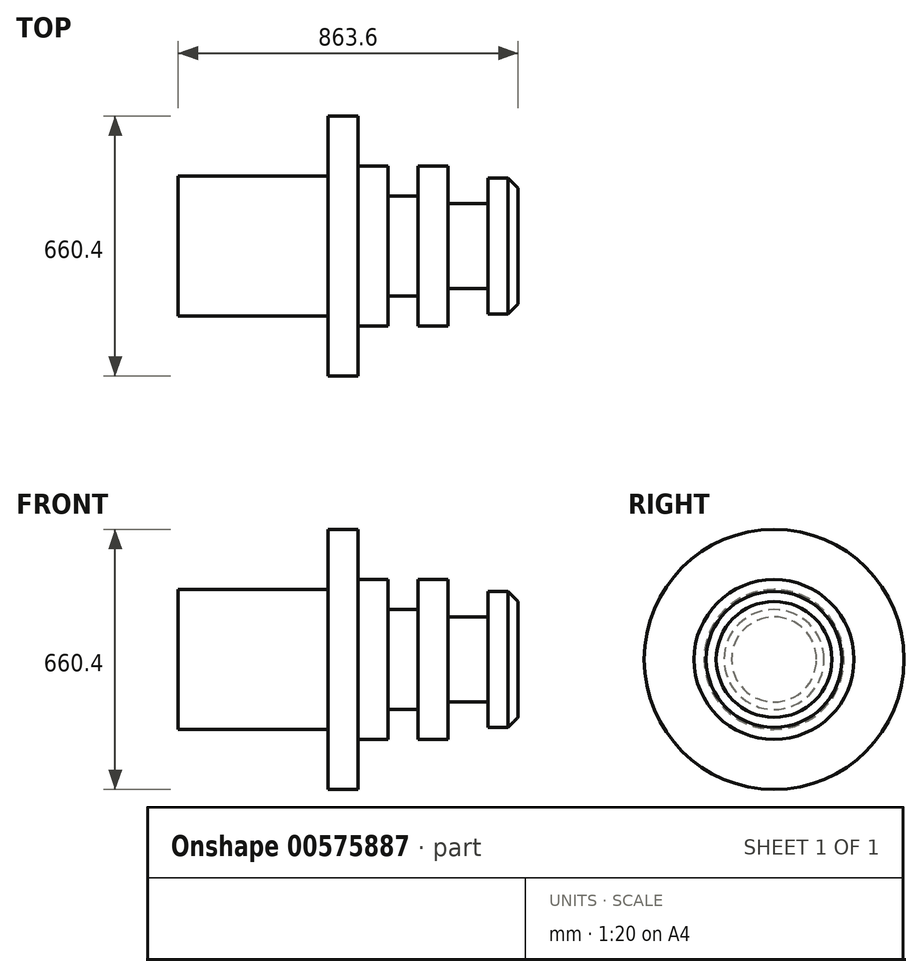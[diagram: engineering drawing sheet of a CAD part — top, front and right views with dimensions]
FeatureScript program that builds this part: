
annotation { "Feature Type Name" : "Feature", "Feature Type Description" : "" }
export const myFeature = defineFeature(function(context is Context, id is Id, definition is map)
    precondition{}
    {
        {
            var Q0;
            Q0=qCreatedBy(makeId("Front.planeOp"),FACE);
            var sketch = newSketch(context, id + "F0", { "sketchPlane" : qUnion([Q0])});
            skLineSegment(sketch, "E0", {"start": v(0, 0) * mm, "end": v(0, 177.8) * mm});
            skLineSegment(sketch, "E1", {"start": v(0, 0) * mm, "end": v(863.6, 0) * mm});
            skLineSegment(sketch, "E2", {"start": v(0, 177.8) * mm, "end": v(381, 177.8) * mm});
            skLineSegment(sketch, "E3", {"start": v(381, 177.8) * mm, "end": v(381, 330.2) * mm});
            skLineSegment(sketch, "E4", {"start": v(381, 330.2) * mm, "end": v(457.2, 330.2) * mm});
            skLineSegment(sketch, "E5", {"start": v(457.2, 330.2) * mm, "end": v(457.2, 203.2) * mm});
            skLineSegment(sketch, "E6", {"start": v(457.2, 203.2) * mm, "end": v(533.4, 203.2) * mm});
            skLineSegment(sketch, "E7", {"start": v(533.4, 203.2) * mm, "end": v(533.4, 127) * mm});
            skLineSegment(sketch, "E8", {"start": v(533.4, 127) * mm, "end": v(609.6, 127) * mm});
            skLineSegment(sketch, "E9", {"start": v(609.6, 127) * mm, "end": v(609.6, 203.2) * mm});
            skLineSegment(sketch, "E10", {"start": v(609.6, 203.2) * mm, "end": v(685.8, 203.2) * mm});
            skLineSegment(sketch, "E11", {"start": v(685.8, 203.2) * mm, "end": v(685.8, 107.95) * mm});
            skLineSegment(sketch, "E12", {"start": v(685.8, 107.95) * mm, "end": v(787.4, 107.95) * mm});
            skLineSegment(sketch, "E13", {"start": v(787.4, 107.95) * mm, "end": v(787.4, 172.45) * mm});
            skLineSegment(sketch, "E14", {"start": v(787.4, 172.45) * mm, "end": v(863.6, 172.45) * mm});
            skLineSegment(sketch, "E15", {"start": v(863.6, 172.45) * mm, "end": v(863.6, 0) * mm});
            skSolve(sketch);
        }
        {
            var Q0;
            Q0=makeQuery(id+"F0.imprint","IMPRINT",FACE,{"disambiguationData":[TD([[makeQuery(id+"F0.imprint","IMPRINT",EDGE,{"derivedFrom":sQuery(id+"F0.wireOp",EDGE,"E0")}),-1.0]])]});
            var Q1;
            Q1=sQuery(id+"F0.wireOp",EDGE,"E1");
            revolve(context, id + "F1", {"entities" : qUnion([Q0]), "axis" : qUnion([Q1]), "revolveType" : RevolveType.FULL});
        }
        {
            var Q0;
            Q0=makeQuery(id+"F1.opRevolve","SWEPT_EDGE",EDGE,{"disambiguationData":[OSD([sQuery(id+"F0.wireOp",EDGE,"E14"),sQuery(id+"F0.wireOp",EDGE,"E15")])]});
            chamfer(context, id + "F2", {"entities" : qUnion([Q0]), "width" : 25.4 * mm, "tangentPropagation" : true});
        }
    });
